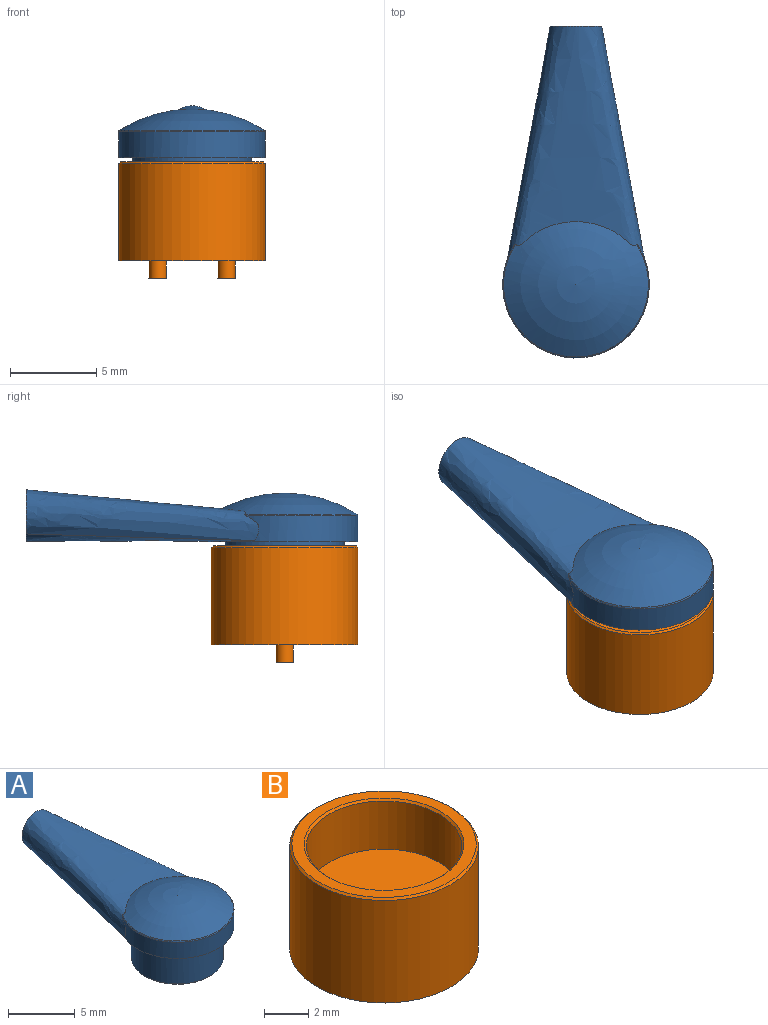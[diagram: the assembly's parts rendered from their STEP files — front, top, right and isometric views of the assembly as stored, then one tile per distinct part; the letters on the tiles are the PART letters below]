
ASSEMBLY  parts=2 mates=1
PART A: 10 faces, bbox 9.2x19.6x6 mm
  f0: cylinder r=3.45mm len=6.9mm, axis (0,0,1), area 62.9mm2, adj f2,f4
  f1: plane 6.7x6.7mm, normal (0,0,-1), area 35.3mm2, adj f2
  f2: cone r=3.45mm half-angle=45deg, axis (0,0,1), area 3mm2, adj f0,f1
  f3: sphere r=7.81mm, area 56.2mm2, adj f6,f9
  f4: plane 8.5x8.5mm, normal (0,0,-1), area 19.4mm2, adj f0,f5
  f5: cylinder r=4.25mm len=8.5mm, axis (0,0,1), area 25.4mm2, adj f4,f6,f7,f9
  f6: bspline ~15x8.5mm, area 106.9mm2, adj f3,f5,f7,f8,f9
  f7: bspline ~13.27x7.76mm, area 57mm2, adj f5,f6,f8
  f8: plane 3.05x3.02mm, normal (0,1,0), area 7.1mm2, adj f6,f7
  f9: torus R=4.15mm, axis (0,0,-1), area 1.8mm2, adj f3,f5,f6
PART B: 11 faces, bbox 8.5x8.5x6.8 mm
  f0: cylinder r=4.25mm len=8.5mm, axis (0,0,-1), area 150.9mm2, adj f1,f9
  f1: plane 8.5x8.5mm, normal (0,0,-1), area 55.2mm2, adj f0,f5,f7
  f2: cylinder r=3.5mm len=7mm, axis (0,0,-1), area 58.3mm2, adj f4,f10
  f3: plane 8.3x8.3mm, normal (0,0,1), area 13.4mm2, adj f9,f10
  f4: plane 7x7mm, normal (0,0,1), area 38.5mm2, adj f2
  f5: cylinder r=0.5mm len=1mm, axis (0,0,1), area 3.1mm2, adj f1,f6
  f6: plane 1x1mm, normal (0,0,-1), area 0.8mm2, adj f5
  f7: cylinder r=0.5mm len=1mm, axis (0,0,1), area 3.1mm2, adj f1,f8
  f8: plane 1x1mm, normal (0,0,-1), area 0.8mm2, adj f7
  f9: cone r=4.15mm half-angle=45deg, axis (0,0,-1), area 3.7mm2, adj f0,f3
  f10: cone r=3.5mm half-angle=45deg, axis (0,0,1), area 3.2mm2, adj f2,f3
PLACE A t=(0,0,6)mm
PLACE B at identity fixed
MATE fastened A.f0 <-> B.f0  axis (0,0,-1) through (0,0,3)mm
